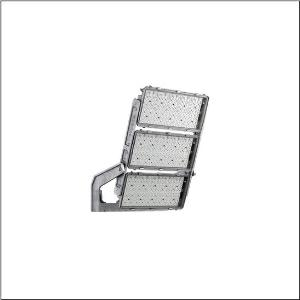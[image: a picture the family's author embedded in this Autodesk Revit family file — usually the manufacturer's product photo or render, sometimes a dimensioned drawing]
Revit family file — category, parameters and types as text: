
# Revit family: floodlight_fl_11_maxi_pro_remote___pl33tblc_5xa779426h01aa_354a
name_source: partatom
category: Lighting Fixtures
units: mm (PartAtom-declared; Revit-internal decimal feet)

## family parameters
Cut with Voids When Loaded = No
Host = Face
Light Source = No
Part Type = Normal
Room Calculation Point = No
Round Connector Dimension = Use Diameter
Shared = No

## types (1)
- --- (1 x LED, 124720 lm, 1388.3 W, 4000K)
    Apparent Load = 1388 VA
    CIE Flux Codes = 24 77 100 100 100
    Color Rendering = 70
    Color Temperature = 4000K
    Default Elevation = 1800 mm
    Description = Floodlight FL 11  maxi  pro Remote floodlight; light control with lens of PMMA; cover panel of toughened safety glass, transparent; light distribution: PL33TBLC, asymmetric direct distribution, LEDcolour temperature: 4000K, rated luminous flux: 124.720lm, colour rendering: CRI > 70, light colour: 740; luminous efficacy: 90lm/W; brightness control: DALI 2 (1 DALI address); with terminal, 8-pole, max. 2.5mm², mains connection: 220..240V/380..400V AC, 50/60Hz, surge voltage resistance: line to ground: 10kV, ECG replaceable separately, LED unit replaceable without ESD environment, dustproof LED module, dimming range 10..100%, no afterglow with DALI off / DMX off command; 1388W floodlight with 2x LED unit of diecast aluminium, coated grey; length: 713mm / width: 651mm / height: 338mm; mounting bracket, of diecast aluminium, uncoated, natural, equipment: Power, protection rating (complete): IP66; insulation class (complete): insulation class I (protective earthing); certification: CE, ENEC, VDE; ball protection: ball impact resistance with accessories, impact resistance: IK07; rated ambient temperature 10°C, only for outdoor installations, permissible operating ambient temperature: -40..+30°C, permissible storage temperature: -40..+85°C; packaging unit: 1 piece

Light Distribution: PL33TBLC
    Height = 320 mm
    Lamp = 1 x LED
    Lamp Light Flux = 124720 lm
    Lamp Power = 1388.3 W
    Lamp count = 1
    Length = 1002 mm
    Luminous efficacy = 90 lm/W
    Manufacturer = Siteco
    ModVariant = No
    Model = 5XA779426H01AA
    Mounting Place = Ceiling
    Mounting Type = Surface mounted
    Number of Poles = 1
    OnlyDefault = Yes
    Power Factor = 1
    Product Name = Floodlight FL 11 maxi pro Remote | PL33TBLC
    Product group = floodlight | ceiling mounted
    ProductGroupID = 302
    Protection Class = Protection class I
    Protection Degree = IP 66
    RLX_Detail_Level = 1
    RLX_Emergency_Light_Flux = 0 lm
    RLX_Emergency_Type = 0
    RLX_Emergency_Type_DB = No
    RlxData = <blob elided: 52165 chars, md5=2a3c10f4>
    Socket = socket
    Standby Power = 0 W
    System Light Flux = 124720 lm
    System Power = 1388 W
    Type Comments = factory setting: luminous flux: 100 % | dim-lin: 254 | 955 mA
    Type Image = l_1006784.jpg
    URL = http://relux.com
    VarID = @adj_026469
    Voltage = 0 V
    Weight = 0.00 kg
    Width = 655 mm

## geometry (parser evidence)
native form markers: Blend x4, Sweep x13
no freeform markers — native parametric forms only
